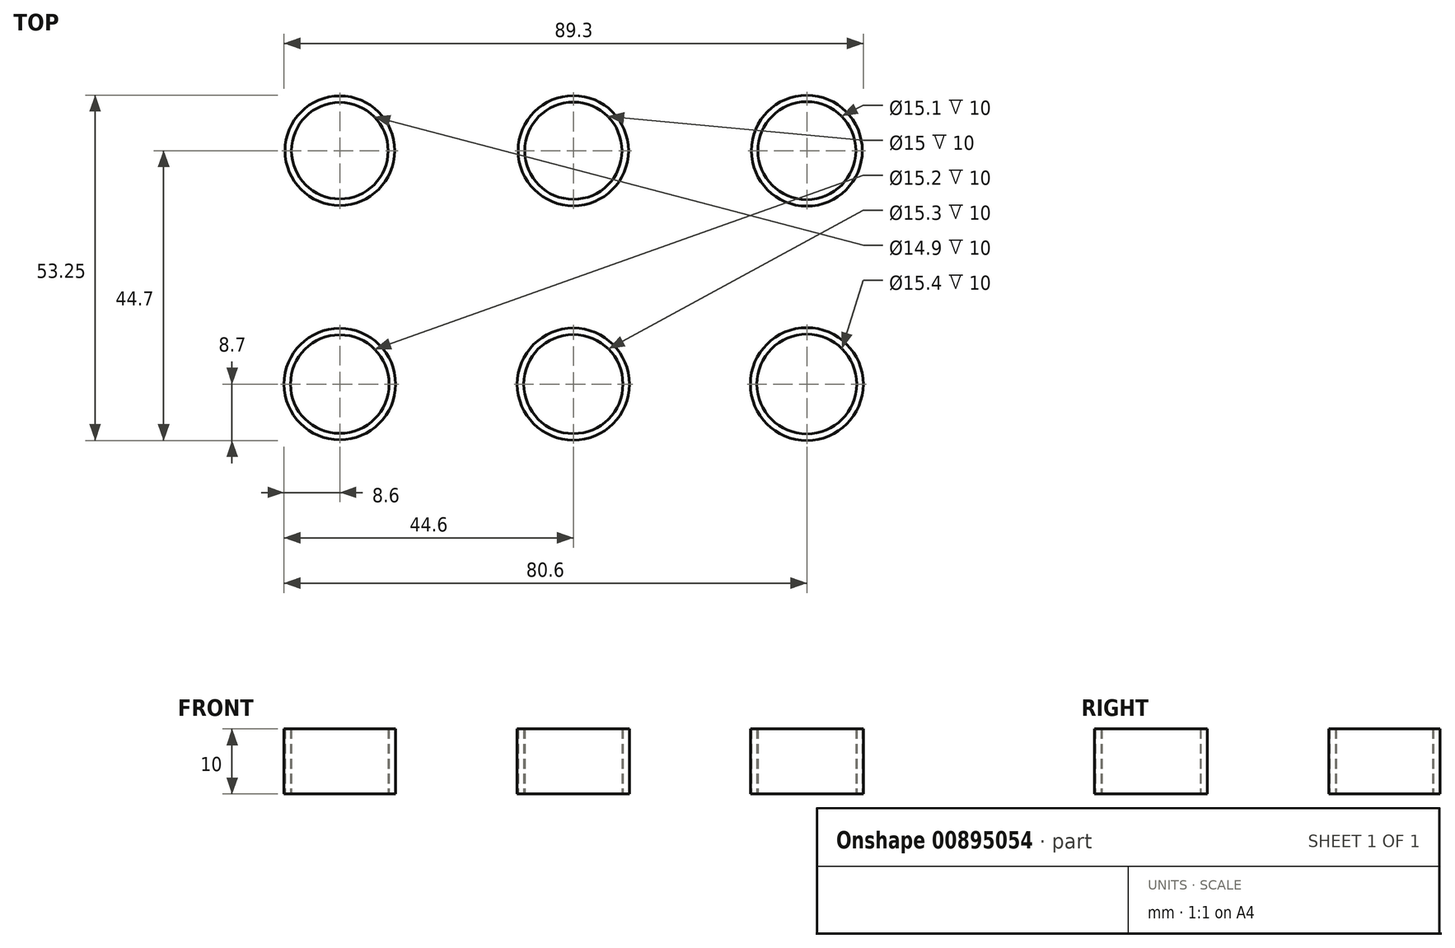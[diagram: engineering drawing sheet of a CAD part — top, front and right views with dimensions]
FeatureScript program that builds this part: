
annotation { "Feature Type Name" : "Feature", "Feature Type Description" : "" }
export const myFeature = defineFeature(function(context is Context, id is Id, definition is map)
    precondition{}
    {
        {
            var Q0;
            Q0=qCreatedBy(makeId("Top.planeOp"),FACE);
            var sketch = newSketch(context, id + "F0", { "sketchPlane" : qUnion([Q0])});
            skLineSegment(sketch, "E0.bottom", {"start": v(90, 90) * mm, "end": v(-90, 90) * mm, "construction": true});
            skLineSegment(sketch, "E0.top", {"start": v(90, -90) * mm, "end": v(-90, -90) * mm, "construction": true});
            skLineSegment(sketch, "E0.left", {"start": v(90, 90) * mm, "end": v(90, -90) * mm, "construction": true});
            skLineSegment(sketch, "E0.right", {"start": v(-90, 90) * mm, "end": v(-90, -90) * mm, "construction": true});
            skPoint(sketch, "E0.middle", {"position": v(0, 0) * mm});
            skCircle(sketch, "E1", {"center": v(0, 0) * mm, "radius": 7.65 * mm});
            skCircle(sketch, "E2.0.1.0", {"center": v(0, 36) * mm, "radius": 7.5 * mm});
            skCircle(sketch, "E2.1.0.0", {"center": v(36, 0) * mm, "radius": 7.7 * mm});
            skCircle(sketch, "E2.1.1.0", {"center": v(36, 36) * mm, "radius": 7.55 * mm});
            skLineSegment(sketch, "E2.direction1", {"start": v(0, 0) * mm, "end": v(36, 0) * mm, "construction": true});
            skLineSegment(sketch, "E2.direction2", {"start": v(0, 0) * mm, "end": v(0, 36) * mm, "construction": true});
            skCircle(sketch, "E3.MirrorC", {"center": v(-36, 36) * mm, "radius": 7.45 * mm});
            skCircle(sketch, "E4.MirrorC", {"center": v(-36, 0) * mm, "radius": 7.6 * mm});
            skCircle(sketch, "E5.0", {"center": v(-36, 36) * mm, "radius": 8.45 * mm});
            skCircle(sketch, "E6.0", {"center": v(0, 36) * mm, "radius": 8.5 * mm});
            skCircle(sketch, "E7.0", {"center": v(36, 36) * mm, "radius": 8.55 * mm});
            skCircle(sketch, "E8.0", {"center": v(-36, 0) * mm, "radius": 8.6 * mm});
            skCircle(sketch, "E9.0", {"center": v(0, 0) * mm, "radius": 8.65 * mm});
            skCircle(sketch, "E10.0", {"center": v(36, 0) * mm, "radius": 8.7 * mm});
            skSolve(sketch);
        }
        {
            var Q0;
            Q0=qSketchRegion(id+"F0",true);
            extrude(context, id + "F1", {"entities" : qUnion([Q0]), "depth" : 10 * mm, "offsetDistance" : 25 * mm});
        }
    });
